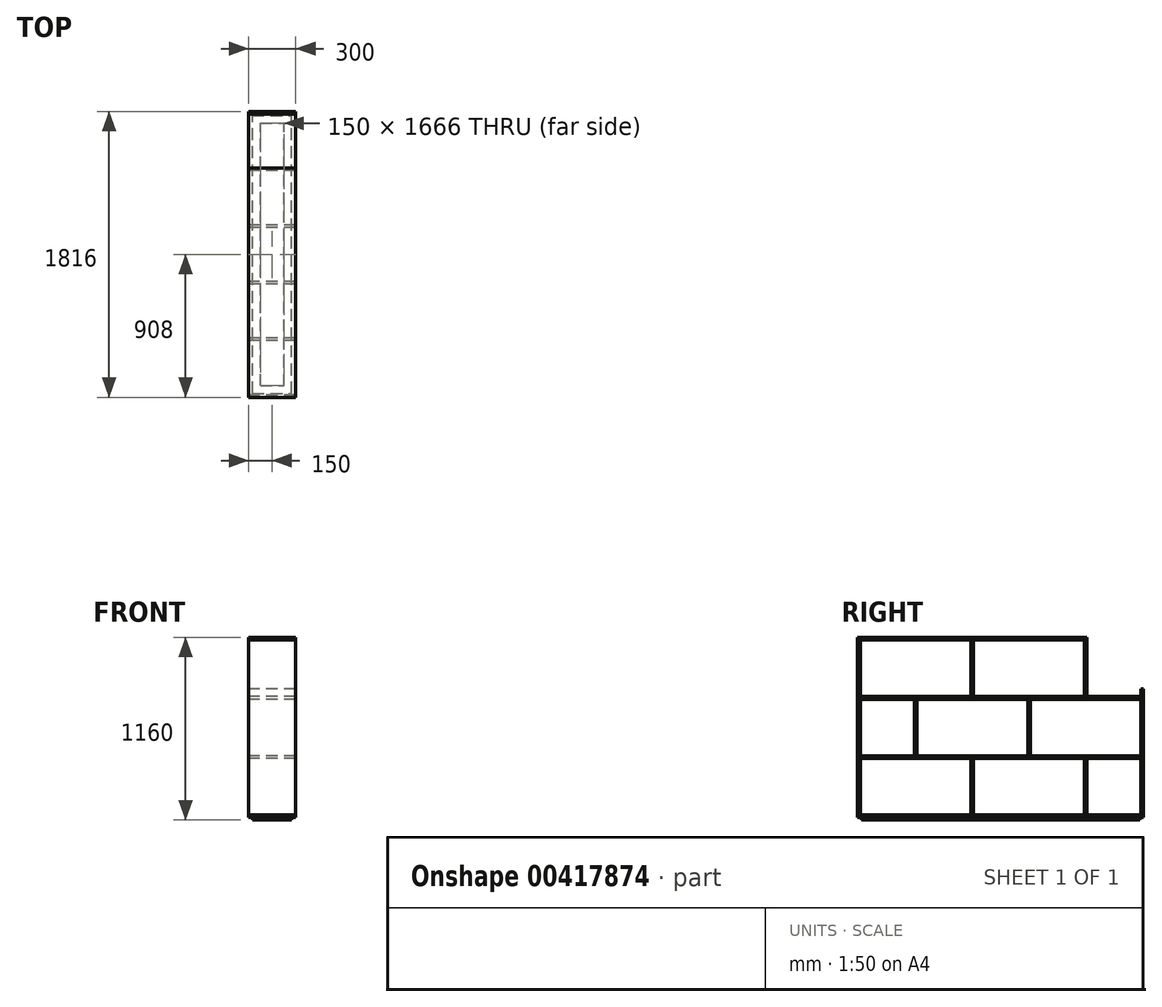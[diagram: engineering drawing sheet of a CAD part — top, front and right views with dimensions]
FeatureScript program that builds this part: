
annotation { "Feature Type Name" : "Feature", "Feature Type Description" : "" }
export const myFeature = defineFeature(function(context is Context, id is Id, definition is map)
    precondition{}
    {
        {
            var Q0;
            Q0=qCreatedBy(makeId("Right.planeOp"),FACE);
            var sketch = newSketch(context, id + "F0", { "sketchPlane" : qUnion([Q0])});
            skLineSegment(sketch, "E0.bottom", {"start": v(0, 0) * mm, "end": v(1816, 0) * mm});
            skLineSegment(sketch, "E0.top", {"start": v(0, 16) * mm, "end": v(1816, 16) * mm});
            skLineSegment(sketch, "E0.left", {"start": v(0, 0) * mm, "end": v(0, 16) * mm});
            skLineSegment(sketch, "E0.right", {"start": v(1816, 0) * mm, "end": v(1816, 16) * mm});
            skLineSegment(sketch, "E1.bottom", {"start": v(0, 376) * mm, "end": v(1816, 376) * mm});
            skLineSegment(sketch, "E1.top", {"start": v(0, 392) * mm, "end": v(1816, 392) * mm});
            skLineSegment(sketch, "E1.left", {"start": v(0, 376) * mm, "end": v(0, 392) * mm});
            skLineSegment(sketch, "E1.right", {"start": v(1816, 376) * mm, "end": v(1816, 392) * mm});
            skLineSegment(sketch, "E2.bottom", {"start": v(0, 752) * mm, "end": v(1816, 752) * mm});
            skLineSegment(sketch, "E2.top", {"start": v(0, 768) * mm, "end": v(1816, 768) * mm});
            skLineSegment(sketch, "E2.left", {"start": v(0, 752) * mm, "end": v(0, 768) * mm});
            skLineSegment(sketch, "E2.right", {"start": v(1816, 752) * mm, "end": v(1816, 768) * mm});
            skLineSegment(sketch, "E3.bottom", {"start": v(0, 1128) * mm, "end": v(1456, 1128) * mm});
            skLineSegment(sketch, "E3.top", {"start": v(0, 1144) * mm, "end": v(1456, 1144) * mm});
            skLineSegment(sketch, "E3.left", {"start": v(0, 1128) * mm, "end": v(0, 1144) * mm});
            skLineSegment(sketch, "E3.right", {"start": v(1456, 1128) * mm, "end": v(1456, 1144) * mm});
            skSolve(sketch);
        }
        {
            var Q0;
            Q0=qCreatedBy(makeId("Right.planeOp"),FACE);
            var sketch = newSketch(context, id + "F1", { "sketchPlane" : qUnion([Q0])});
            skLineSegment(sketch, "E4.bottom", {"start": v(1800, 16) * mm, "end": v(1816, 16) * mm});
            skLineSegment(sketch, "E4.top", {"start": v(1800, 818) * mm, "end": v(1816, 818) * mm});
            skLineSegment(sketch, "E4.left", {"start": v(1800, 16) * mm, "end": v(1800, 818) * mm});
            skLineSegment(sketch, "E4.right", {"start": v(1816, 16) * mm, "end": v(1816, 818) * mm});
            skLineSegment(sketch, "E5.bottom", {"start": v(0, 16) * mm, "end": v(16, 16) * mm});
            skLineSegment(sketch, "E5.top", {"start": v(0, 1128) * mm, "end": v(16, 1128) * mm});
            skLineSegment(sketch, "E5.left", {"start": v(0, 16) * mm, "end": v(0, 1128) * mm});
            skLineSegment(sketch, "E5.right", {"start": v(16, 16) * mm, "end": v(16, 1128) * mm});
            skLineSegment(sketch, "E6.bottom", {"start": v(1456, 1128) * mm, "end": v(1440, 1128) * mm});
            skLineSegment(sketch, "E6.top", {"start": v(1456, 768) * mm, "end": v(1440, 768) * mm});
            skLineSegment(sketch, "E6.left", {"start": v(1456, 1128) * mm, "end": v(1456, 768) * mm});
            skLineSegment(sketch, "E6.right", {"start": v(1440, 1128) * mm, "end": v(1440, 768) * mm});
            skLineSegment(sketch, "E7.bottom", {"start": v(1080, 752) * mm, "end": v(1096, 752) * mm});
            skLineSegment(sketch, "E7.top", {"start": v(1080, 392) * mm, "end": v(1096, 392) * mm});
            skLineSegment(sketch, "E7.left", {"start": v(1080, 752) * mm, "end": v(1080, 392) * mm});
            skLineSegment(sketch, "E7.right", {"start": v(1096, 752) * mm, "end": v(1096, 392) * mm});
            skLineSegment(sketch, "E8.bottom", {"start": v(1440, 376) * mm, "end": v(1456, 376) * mm});
            skLineSegment(sketch, "E8.top", {"start": v(1440, 16) * mm, "end": v(1456, 16) * mm});
            skLineSegment(sketch, "E8.left", {"start": v(1440, 376) * mm, "end": v(1440, 16) * mm});
            skLineSegment(sketch, "E8.right", {"start": v(1456, 376) * mm, "end": v(1456, 16) * mm});
            skLineSegment(sketch, "E9.bottom", {"start": v(720, 376) * mm, "end": v(736, 376) * mm});
            skLineSegment(sketch, "E9.top", {"start": v(720, 16) * mm, "end": v(736, 16) * mm});
            skLineSegment(sketch, "E9.left", {"start": v(720, 376) * mm, "end": v(720, 16) * mm});
            skLineSegment(sketch, "E9.right", {"start": v(736, 376) * mm, "end": v(736, 16) * mm});
            skLineSegment(sketch, "E10.bottom", {"start": v(360, 752) * mm, "end": v(376, 752) * mm});
            skLineSegment(sketch, "E10.top", {"start": v(360, 392) * mm, "end": v(376, 392) * mm});
            skLineSegment(sketch, "E10.left", {"start": v(360, 752) * mm, "end": v(360, 392) * mm});
            skLineSegment(sketch, "E10.right", {"start": v(376, 752) * mm, "end": v(376, 392) * mm});
            skLineSegment(sketch, "E11.bottom", {"start": v(720, 1128) * mm, "end": v(736, 1128) * mm});
            skLineSegment(sketch, "E11.top", {"start": v(720, 768) * mm, "end": v(736, 768) * mm});
            skLineSegment(sketch, "E11.left", {"start": v(720, 1128) * mm, "end": v(720, 768) * mm});
            skLineSegment(sketch, "E11.right", {"start": v(736, 1128) * mm, "end": v(736, 768) * mm});
            skSolve(sketch);
        }
        {
            var Q0;
            Q0=qCreatedBy(makeId("Right.planeOp"),FACE);
            var sketch = newSketch(context, id + "F2", { "sketchPlane" : qUnion([Q0])});
            skLineSegment(sketch, "E12.bottom", {"start": v(0, 0) * mm, "end": v(1816, 0) * mm});
            skLineSegment(sketch, "E12.top", {"start": v(0, 16) * mm, "end": v(1816, 16) * mm});
            skLineSegment(sketch, "E12.left", {"start": v(0, 0) * mm, "end": v(0, 16) * mm});
            skLineSegment(sketch, "E12.right", {"start": v(1816, 0) * mm, "end": v(1816, 16) * mm});
            skLineSegment(sketch, "E13.bottom", {"start": v(16, 376) * mm, "end": v(1800, 376) * mm});
            skLineSegment(sketch, "E13.top", {"start": v(16, 392) * mm, "end": v(1800, 392) * mm});
            skLineSegment(sketch, "E13.left", {"start": v(16, 376) * mm, "end": v(16, 392) * mm});
            skLineSegment(sketch, "E13.right", {"start": v(1800, 376) * mm, "end": v(1800, 392) * mm});
            skLineSegment(sketch, "E14.bottom", {"start": v(16, 752) * mm, "end": v(1800, 752) * mm});
            skLineSegment(sketch, "E14.top", {"start": v(16, 768) * mm, "end": v(1800, 768) * mm});
            skLineSegment(sketch, "E14.left", {"start": v(16, 752) * mm, "end": v(16, 768) * mm});
            skLineSegment(sketch, "E14.right", {"start": v(1800, 752) * mm, "end": v(1800, 768) * mm});
            skLineSegment(sketch, "E15.bottom", {"start": v(0, 1144) * mm, "end": v(1456, 1144) * mm});
            skLineSegment(sketch, "E15.top", {"start": v(0, 1128) * mm, "end": v(1456, 1128) * mm});
            skLineSegment(sketch, "E15.left", {"start": v(0, 1144) * mm, "end": v(0, 1128) * mm});
            skLineSegment(sketch, "E15.right", {"start": v(1456, 1144) * mm, "end": v(1456, 1128) * mm});
            skSolve(sketch);
        }
        {
            var Q0;
            Q0 = qSketchRegion(id + "F2", true);
            extrude(context, id + "F3", {"entities" : qUnion([Q0]), "depth" : 300 * mm});
        }
        {
            var Q0;
            Q0 = qSketchRegion(id + "F1", true);
            extrude(context, id + "F4", {"entities" : qUnion([Q0]), "depth" : 300 * mm});
        }
        {
            var Q0;
            Q0=qCreatedBy(makeId("Top.planeOp"),FACE);
            var sketch = newSketch(context, id + "F5", { "sketchPlane" : qUnion([Q0])});
            skLineSegment(sketch, "E16.bottom", {"start": v(25, 25) * mm, "end": v(75, 25) * mm});
            skLineSegment(sketch, "E16.top", {"start": v(25, 1791) * mm, "end": v(75, 1791) * mm});
            skLineSegment(sketch, "E16.left", {"start": v(25, 25) * mm, "end": v(25, 1791) * mm});
            skLineSegment(sketch, "E16.right", {"start": v(75, 25) * mm, "end": v(75, 1791) * mm});
            skLineSegment(sketch, "E17.bottom", {"start": v(225, 25) * mm, "end": v(275, 25) * mm});
            skLineSegment(sketch, "E17.top", {"start": v(225, 1791) * mm, "end": v(275, 1791) * mm});
            skLineSegment(sketch, "E17.left", {"start": v(225, 25) * mm, "end": v(225, 1791) * mm});
            skLineSegment(sketch, "E17.right", {"start": v(275, 25) * mm, "end": v(275, 1791) * mm});
            skLineSegment(sketch, "E18.bottom", {"start": v(75, 25) * mm, "end": v(225, 25) * mm});
            skLineSegment(sketch, "E18.top", {"start": v(75, 75) * mm, "end": v(225, 75) * mm});
            skLineSegment(sketch, "E18.left", {"start": v(75, 25) * mm, "end": v(75, 75) * mm});
            skLineSegment(sketch, "E18.right", {"start": v(225, 25) * mm, "end": v(225, 75) * mm});
            skLineSegment(sketch, "E19.bottom", {"start": v(75, 1791) * mm, "end": v(225, 1791) * mm});
            skLineSegment(sketch, "E19.top", {"start": v(75, 1741) * mm, "end": v(225, 1741) * mm});
            skLineSegment(sketch, "E19.left", {"start": v(75, 1791) * mm, "end": v(75, 1741) * mm});
            skLineSegment(sketch, "E19.right", {"start": v(225, 1791) * mm, "end": v(225, 1741) * mm});
            skSolve(sketch);
        }
        {
            var Q0;
            Q0 = qSketchRegion(id + "F5", true);
            extrude(context, id + "F6", {"entities" : qUnion([Q0]), "oppositeDirection" : true, "depth" : 16 * mm});
        }
    });
